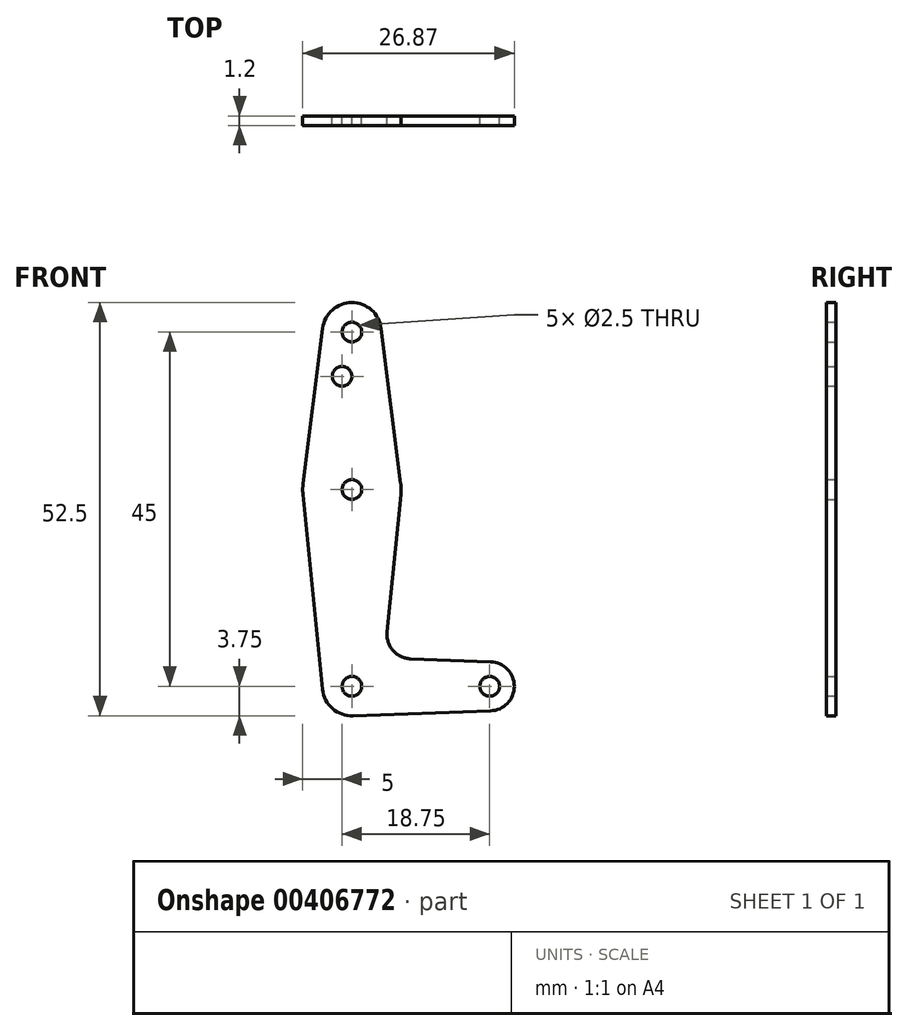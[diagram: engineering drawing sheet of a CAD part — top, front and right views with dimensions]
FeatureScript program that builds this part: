
annotation { "Feature Type Name" : "Feature", "Feature Type Description" : "" }
export const myFeature = defineFeature(function(context is Context, id is Id, definition is map)
    precondition{}
    {
        {
            var Q0;
            Q0=qCreatedBy(makeId("Front.planeOp"),FACE);
            var sketch = newSketch(context, id + "F0", { "sketchPlane" : qUnion([Q0])});
            skLineSegment(sketch, "E0", {"start": v(0, 0) * mm, "end": v(0, 45) * mm, "construction": true});
            skLineSegment(sketch, "E1", {"start": v(0, 0) * mm, "end": v(17.5, 0) * mm, "construction": true});
            skCircle(sketch, "E2", {"center": v(0, 45) * mm, "radius": 3.75 * mm});
            skCircle(sketch, "E3", {"center": v(0, 0) * mm, "radius": 3.75 * mm});
            skCircle(sketch, "E4", {"center": v(17.5, 0) * mm, "radius": 3.12 * mm});
            skCircle(sketch, "E5", {"center": v(0, 25) * mm, "radius": 6.25 * mm});
            skLineSegment(sketch, "E6", {"start": v(-3.72, 45.47) * mm, "end": v(-6.2, 25.78) * mm});
            skLineSegment(sketch, "E7", {"start": v(3.72, 45.47) * mm, "end": v(6.2, 25.78) * mm});
            skLineSegment(sketch, "E8", {"start": v(-3.73, -0.38) * mm, "end": v(-6.22, 24.38) * mm});
            skLineSegment(sketch, "E9", {"start": v(4.47, 6.93) * mm, "end": v(6.22, 24.38) * mm});
            skLineSegment(sketch, "E10", {"start": v(17.61, 3.12) * mm, "end": v(7.47, 3.49) * mm});
            skLineSegment(sketch, "E11", {"start": v(0.13, -3.75) * mm, "end": v(17.61, -3.12) * mm});
            skCircle(sketch, "E12", {"center": v(0, 45) * mm, "radius": 1.25 * mm});
            skCircle(sketch, "E13", {"center": v(0, 25) * mm, "radius": 1.25 * mm});
            skCircle(sketch, "E14", {"center": v(0, 0) * mm, "radius": 1.25 * mm});
            skCircle(sketch, "E15", {"center": v(17.5, 0) * mm, "radius": 1.25 * mm});
            skArc(sketch, "E16.filletArc", {"start": v(4.47, 6.93) * mm, "mid": v(5.22, 4.56) * mm, "end": v(7.47, 3.49) * mm});
            skPoint(sketch, "E17", {"position": v(0, 39.38) * mm});
            skLineSegment(sketch, "E18", {"start": v(0, 39.38) * mm, "end": v(-1.25, 39.38) * mm});
            skCircle(sketch, "E19", {"center": v(-1.25, 39.38) * mm, "radius": 1.25 * mm});
            skSolve(sketch);
        }
        {
            var Q0;
            Q0 = qSketchRegion(id + "F0", true);
            extrude(context, id + "F1", {"entities" : qUnion([Q0]), "depth" : 1.2 * mm});
        }
    });
